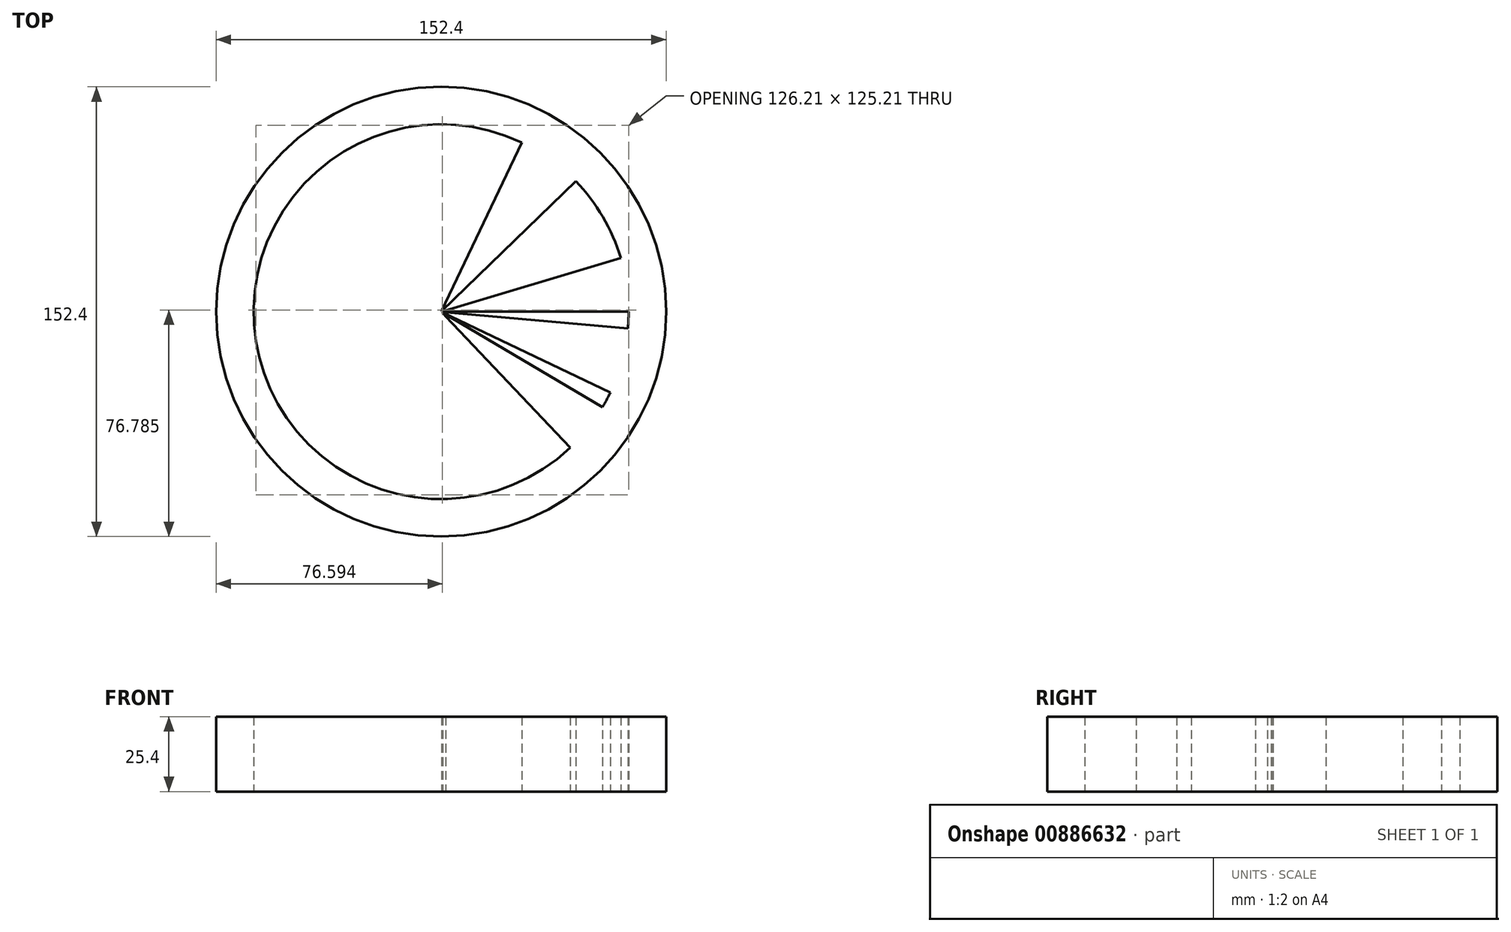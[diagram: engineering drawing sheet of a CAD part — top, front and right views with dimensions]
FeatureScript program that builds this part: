
annotation { "Feature Type Name" : "Feature", "Feature Type Description" : "" }
export const myFeature = defineFeature(function(context is Context, id is Id, definition is map)
    precondition{}
    {
        {
            var Q0;
            Q0=qCreatedBy(makeId("Top.planeOp"),FACE);
            var sketch = newSketch(context, id + "F0", { "sketchPlane" : qUnion([Q0])});
            skCircle(sketch, "E0", {"center": v(0, 0) * mm, "radius": 76.2 * mm});
            skLineSegment(sketch, "E1", {"start": v(0, 76.2) * mm, "end": v(0, -76.2) * mm});
            skLineSegment(sketch, "E2", {"start": v(-76.2, 0) * mm, "end": v(76.2, 0) * mm});
            skLineSegment(sketch, "E3", {"start": v(0, -76.2) * mm, "end": v(76.2, 0) * mm, "construction": true});
            skLineSegment(sketch, "E4", {"start": v(-76.2, 0) * mm, "end": v(0, 76.2) * mm, "construction": true});
            skLineSegment(sketch, "E5", {"start": v(-52.47, 55.26) * mm, "end": v(52.47, -55.26) * mm});
            skLineSegment(sketch, "E6", {"start": v(54.71, 53.04) * mm, "end": v(-54.71, -53.04) * mm});
            skLineSegment(sketch, "E7", {"start": v(26.69, 71.37) * mm, "end": v(-26.69, -71.37) * mm});
            skLineSegment(sketch, "E8", {"start": v(-29.5, 70.26) * mm, "end": v(29.5, -70.26) * mm});
            skLineSegment(sketch, "E9", {"start": v(71.21, 27.12) * mm, "end": v(-71.21, -27.12) * mm});
            skLineSegment(sketch, "E10", {"start": v(-68.73, 32.9) * mm, "end": v(68.73, -32.9) * mm});
            skCircle(sketch, "E11", {"center": v(0, 0) * mm, "radius": 63.5 * mm});
            skLineSegment(sketch, "E12", {"start": v(-59.38, -47.75) * mm, "end": v(59.38, 47.75) * mm});
            skLineSegment(sketch, "E13", {"start": v(-73, -21.87) * mm, "end": v(73, 21.87) * mm});
            skLineSegment(sketch, "E14", {"start": v(-75.9, 6.85) * mm, "end": v(75.9, -6.85) * mm});
            skLineSegment(sketch, "E15", {"start": v(-65.57, 38.81) * mm, "end": v(65.57, -38.81) * mm});
            skLineSegment(sketch, "E16", {"start": v(-46.6, 60.29) * mm, "end": v(46.96, -60.01) * mm});
            skLineSegment(sketch, "E17", {"start": v(-25.62, 71.76) * mm, "end": v(25.62, -71.76) * mm});
            skLineSegment(sketch, "E18", {"start": v(5.1, 76.03) * mm, "end": v(-5.1, -76.03) * mm});
            skLineSegment(sketch, "E19", {"start": v(32.75, 68.8) * mm, "end": v(-32.75, -68.8) * mm});
            skSolve(sketch);
        }
        {
            var Q0;
            {var subQ0=sQuery(id+"F0.wireOp",EDGE,"E5");var subQ1=sQuery(id+"F0.wireOp",EDGE,"E0");var subQ2=makeQuery(id+"F0.imprint","INTERSECT",VERTEX,{"disambiguationData":[OD(0.0)],"derivedFrom":[subQ1,subQ0]});Q0=makeQuery(id+"F0.imprint","IMPRINT",FACE,{"disambiguationData":[TD([[makeQuery(id+"F0.imprint","IMPRINT",EDGE,{"disambiguationData":[TD([[subQ2,-1.0]])],"derivedFrom":subQ1}),1.0]])]});}
            var Q1;
            {var subQ0=sQuery(id+"F0.wireOp",EDGE,"E5");var subQ1=sQuery(id+"F0.wireOp",EDGE,"E0");var subQ2=makeQuery(id+"F0.imprint","INTERSECT",VERTEX,{"disambiguationData":[OD(0.0)],"derivedFrom":[subQ1,subQ0]});Q1=makeQuery(id+"F0.imprint","IMPRINT",FACE,{"disambiguationData":[TD([[makeQuery(id+"F0.imprint","IMPRINT",EDGE,{"disambiguationData":[TD([[subQ2,1.0]])],"derivedFrom":subQ1}),1.0]])]});}
            var Q2;
            {var subQ0=sQuery(id+"F0.wireOp",EDGE,"E8");var subQ1=sQuery(id+"F0.wireOp",EDGE,"E0");var subQ2=makeQuery(id+"F0.imprint","INTERSECT",VERTEX,{"disambiguationData":[OD(0.0)],"derivedFrom":[subQ1,subQ0]});Q2=makeQuery(id+"F0.imprint","IMPRINT",FACE,{"disambiguationData":[TD([[makeQuery(id+"F0.imprint","IMPRINT",EDGE,{"disambiguationData":[TD([[subQ2,-1.0]])],"derivedFrom":subQ1}),1.0]])]});}
            var Q3;
            {var subQ0=sQuery(id+"F0.wireOp",EDGE,"E8");var subQ1=sQuery(id+"F0.wireOp",EDGE,"E0");var subQ2=makeQuery(id+"F0.imprint","INTERSECT",VERTEX,{"disambiguationData":[OD(0.0)],"derivedFrom":[subQ1,subQ0]});Q3=makeQuery(id+"F0.imprint","IMPRINT",FACE,{"disambiguationData":[TD([[makeQuery(id+"F0.imprint","IMPRINT",EDGE,{"disambiguationData":[TD([[subQ2,1.0]])],"derivedFrom":subQ1}),1.0]])]});}
            var Q4;
            {var subQ0=sQuery(id+"F0.wireOp",EDGE,"E1");var subQ1=sQuery(id+"F0.wireOp",EDGE,"E0");var subQ2=makeQuery(id+"F0.imprint","INTERSECT",VERTEX,{"disambiguationData":[OD(0.0)],"derivedFrom":[subQ1,subQ0]});Q4=makeQuery(id+"F0.imprint","IMPRINT",FACE,{"disambiguationData":[TD([[makeQuery(id+"F0.imprint","IMPRINT",EDGE,{"disambiguationData":[TD([[subQ2,-1.0]])],"derivedFrom":subQ1}),1.0]])]});}
            var Q5;
            {var subQ0=sQuery(id+"F0.wireOp",EDGE,"E1");var subQ1=sQuery(id+"F0.wireOp",EDGE,"E0");var subQ2=makeQuery(id+"F0.imprint","INTERSECT",VERTEX,{"disambiguationData":[OD(0.0)],"derivedFrom":[subQ1,subQ0]});Q5=makeQuery(id+"F0.imprint","IMPRINT",FACE,{"disambiguationData":[TD([[makeQuery(id+"F0.imprint","IMPRINT",EDGE,{"disambiguationData":[TD([[subQ2,1.0]])],"derivedFrom":subQ1}),1.0]])]});}
            var Q6;
            {var subQ0=sQuery(id+"F0.wireOp",EDGE,"E7");var subQ1=sQuery(id+"F0.wireOp",EDGE,"E0");var subQ2=makeQuery(id+"F0.imprint","INTERSECT",VERTEX,{"disambiguationData":[OD(0.0)],"derivedFrom":[subQ1,subQ0]});Q6=makeQuery(id+"F0.imprint","IMPRINT",FACE,{"disambiguationData":[TD([[makeQuery(id+"F0.imprint","IMPRINT",EDGE,{"disambiguationData":[TD([[subQ2,-1.0]])],"derivedFrom":subQ1}),1.0]])]});}
            var Q7;
            {var subQ0=sQuery(id+"F0.wireOp",EDGE,"E7");var subQ1=sQuery(id+"F0.wireOp",EDGE,"E0");var subQ2=makeQuery(id+"F0.imprint","INTERSECT",VERTEX,{"disambiguationData":[OD(0.0)],"derivedFrom":[subQ1,subQ0]});Q7=makeQuery(id+"F0.imprint","IMPRINT",FACE,{"disambiguationData":[TD([[makeQuery(id+"F0.imprint","IMPRINT",EDGE,{"disambiguationData":[TD([[subQ2,1.0]])],"derivedFrom":subQ1}),1.0]])]});}
            var Q8;
            {var subQ0=sQuery(id+"F0.wireOp",EDGE,"E6");var subQ1=sQuery(id+"F0.wireOp",EDGE,"E0");var subQ2=makeQuery(id+"F0.imprint","INTERSECT",VERTEX,{"disambiguationData":[OD(0.0)],"derivedFrom":[subQ1,subQ0]});Q8=makeQuery(id+"F0.imprint","IMPRINT",FACE,{"disambiguationData":[TD([[makeQuery(id+"F0.imprint","IMPRINT",EDGE,{"disambiguationData":[TD([[subQ2,-1.0]])],"derivedFrom":subQ1}),1.0]])]});}
            var Q9;
            {var subQ0=sQuery(id+"F0.wireOp",EDGE,"E6");var subQ1=sQuery(id+"F0.wireOp",EDGE,"E0");var subQ2=makeQuery(id+"F0.imprint","INTERSECT",VERTEX,{"disambiguationData":[OD(0.0)],"derivedFrom":[subQ1,subQ0]});Q9=makeQuery(id+"F0.imprint","IMPRINT",FACE,{"disambiguationData":[TD([[makeQuery(id+"F0.imprint","IMPRINT",EDGE,{"disambiguationData":[TD([[subQ2,1.0]])],"derivedFrom":subQ1}),1.0]])]});}
            var Q10;
            {var subQ0=sQuery(id+"F0.wireOp",EDGE,"E9");var subQ1=sQuery(id+"F0.wireOp",EDGE,"E0");var subQ2=makeQuery(id+"F0.imprint","INTERSECT",VERTEX,{"disambiguationData":[OD(0.0)],"derivedFrom":[subQ1,subQ0]});Q10=makeQuery(id+"F0.imprint","IMPRINT",FACE,{"disambiguationData":[TD([[makeQuery(id+"F0.imprint","IMPRINT",EDGE,{"disambiguationData":[TD([[subQ2,-1.0]])],"derivedFrom":subQ1}),1.0]])]});}
            var Q11;
            {var subQ0=sQuery(id+"F0.wireOp",EDGE,"E9");var subQ1=sQuery(id+"F0.wireOp",EDGE,"E0");var subQ2=makeQuery(id+"F0.imprint","INTERSECT",VERTEX,{"disambiguationData":[OD(0.0)],"derivedFrom":[subQ1,subQ0]});Q11=makeQuery(id+"F0.imprint","IMPRINT",FACE,{"disambiguationData":[TD([[makeQuery(id+"F0.imprint","IMPRINT",EDGE,{"disambiguationData":[TD([[subQ2,1.0]])],"derivedFrom":subQ1}),1.0]])]});}
            var Q12;
            {var subQ0=sQuery(id+"F0.wireOp",EDGE,"E2");var subQ1=sQuery(id+"F0.wireOp",EDGE,"E0");var subQ2=makeQuery(id+"F0.imprint","INTERSECT",VERTEX,{"disambiguationData":[OD(1.0)],"derivedFrom":[subQ1,subQ0]});Q12=makeQuery(id+"F0.imprint","IMPRINT",FACE,{"disambiguationData":[TD([[makeQuery(id+"F0.imprint","IMPRINT",EDGE,{"disambiguationData":[TD([[subQ2,-1.0]])],"derivedFrom":subQ1}),1.0]])]});}
            var Q13;
            {var subQ0=sQuery(id+"F0.wireOp",EDGE,"E2");var subQ1=sQuery(id+"F0.wireOp",EDGE,"E0");var subQ2=makeQuery(id+"F0.imprint","INTERSECT",VERTEX,{"disambiguationData":[OD(1.0)],"derivedFrom":[subQ1,subQ0]});Q13=makeQuery(id+"F0.imprint","IMPRINT",FACE,{"disambiguationData":[TD([[makeQuery(id+"F0.imprint","IMPRINT",EDGE,{"disambiguationData":[TD([[subQ2,1.0]])],"derivedFrom":subQ1}),1.0]])]});}
            var Q14;
            {var subQ0=sQuery(id+"F0.wireOp",EDGE,"E10");var subQ1=sQuery(id+"F0.wireOp",EDGE,"E0");var subQ2=makeQuery(id+"F0.imprint","INTERSECT",VERTEX,{"disambiguationData":[OD(1.0)],"derivedFrom":[subQ1,subQ0]});Q14=makeQuery(id+"F0.imprint","IMPRINT",FACE,{"disambiguationData":[TD([[makeQuery(id+"F0.imprint","IMPRINT",EDGE,{"disambiguationData":[TD([[subQ2,-1.0]])],"derivedFrom":subQ1}),1.0]])]});}
            var Q15;
            {var subQ0=sQuery(id+"F0.wireOp",EDGE,"E10");var subQ1=sQuery(id+"F0.wireOp",EDGE,"E0");var subQ2=makeQuery(id+"F0.imprint","INTERSECT",VERTEX,{"disambiguationData":[OD(1.0)],"derivedFrom":[subQ1,subQ0]});Q15=makeQuery(id+"F0.imprint","IMPRINT",FACE,{"disambiguationData":[TD([[makeQuery(id+"F0.imprint","IMPRINT",EDGE,{"disambiguationData":[TD([[subQ2,1.0]])],"derivedFrom":subQ1}),1.0]])]});}
            var Q16;
            {var subQ0=sQuery(id+"F0.wireOp",EDGE,"E5");var subQ1=sQuery(id+"F0.wireOp",EDGE,"E0");var subQ2=makeQuery(id+"F0.imprint","INTERSECT",VERTEX,{"disambiguationData":[OD(1.0)],"derivedFrom":[subQ1,subQ0]});Q16=makeQuery(id+"F0.imprint","IMPRINT",FACE,{"disambiguationData":[TD([[makeQuery(id+"F0.imprint","IMPRINT",EDGE,{"disambiguationData":[TD([[subQ2,-1.0]])],"derivedFrom":subQ1}),1.0]])]});}
            var Q17;
            {var subQ0=sQuery(id+"F0.wireOp",EDGE,"E5");var subQ1=sQuery(id+"F0.wireOp",EDGE,"E0");var subQ2=makeQuery(id+"F0.imprint","INTERSECT",VERTEX,{"disambiguationData":[OD(1.0)],"derivedFrom":[subQ1,subQ0]});Q17=makeQuery(id+"F0.imprint","IMPRINT",FACE,{"disambiguationData":[TD([[makeQuery(id+"F0.imprint","IMPRINT",EDGE,{"disambiguationData":[TD([[subQ2,1.0]])],"derivedFrom":subQ1}),1.0]])]});}
            var Q18;
            {var subQ0=sQuery(id+"F0.wireOp",EDGE,"E8");var subQ1=sQuery(id+"F0.wireOp",EDGE,"E0");var subQ2=makeQuery(id+"F0.imprint","INTERSECT",VERTEX,{"disambiguationData":[OD(1.0)],"derivedFrom":[subQ1,subQ0]});Q18=makeQuery(id+"F0.imprint","IMPRINT",FACE,{"disambiguationData":[TD([[makeQuery(id+"F0.imprint","IMPRINT",EDGE,{"disambiguationData":[TD([[subQ2,-1.0]])],"derivedFrom":subQ1}),1.0]])]});}
            var Q19;
            {var subQ0=sQuery(id+"F0.wireOp",EDGE,"E8");var subQ1=sQuery(id+"F0.wireOp",EDGE,"E0");var subQ2=makeQuery(id+"F0.imprint","INTERSECT",VERTEX,{"disambiguationData":[OD(1.0)],"derivedFrom":[subQ1,subQ0]});Q19=makeQuery(id+"F0.imprint","IMPRINT",FACE,{"disambiguationData":[TD([[makeQuery(id+"F0.imprint","IMPRINT",EDGE,{"disambiguationData":[TD([[subQ2,1.0]])],"derivedFrom":subQ1}),1.0]])]});}
            var Q20;
            {var subQ0=sQuery(id+"F0.wireOp",EDGE,"E1");var subQ1=sQuery(id+"F0.wireOp",EDGE,"E0");var subQ2=makeQuery(id+"F0.imprint","INTERSECT",VERTEX,{"disambiguationData":[OD(1.0)],"derivedFrom":[subQ1,subQ0]});Q20=makeQuery(id+"F0.imprint","IMPRINT",FACE,{"disambiguationData":[TD([[makeQuery(id+"F0.imprint","IMPRINT",EDGE,{"disambiguationData":[TD([[subQ2,-1.0]])],"derivedFrom":subQ1}),1.0]])]});}
            var Q21;
            {var subQ0=sQuery(id+"F0.wireOp",EDGE,"E1");var subQ1=sQuery(id+"F0.wireOp",EDGE,"E0");var subQ2=makeQuery(id+"F0.imprint","INTERSECT",VERTEX,{"disambiguationData":[OD(1.0)],"derivedFrom":[subQ1,subQ0]});Q21=makeQuery(id+"F0.imprint","IMPRINT",FACE,{"disambiguationData":[TD([[makeQuery(id+"F0.imprint","IMPRINT",EDGE,{"disambiguationData":[TD([[subQ2,1.0]])],"derivedFrom":subQ1}),1.0]])]});}
            var Q22;
            {var subQ0=sQuery(id+"F0.wireOp",EDGE,"E7");var subQ1=sQuery(id+"F0.wireOp",EDGE,"E0");var subQ2=makeQuery(id+"F0.imprint","INTERSECT",VERTEX,{"disambiguationData":[OD(1.0)],"derivedFrom":[subQ1,subQ0]});Q22=makeQuery(id+"F0.imprint","IMPRINT",FACE,{"disambiguationData":[TD([[makeQuery(id+"F0.imprint","IMPRINT",EDGE,{"disambiguationData":[TD([[subQ2,-1.0]])],"derivedFrom":subQ1}),1.0]])]});}
            var Q23;
            {var subQ0=sQuery(id+"F0.wireOp",EDGE,"E7");var subQ1=sQuery(id+"F0.wireOp",EDGE,"E0");var subQ2=makeQuery(id+"F0.imprint","INTERSECT",VERTEX,{"disambiguationData":[OD(1.0)],"derivedFrom":[subQ1,subQ0]});Q23=makeQuery(id+"F0.imprint","IMPRINT",FACE,{"disambiguationData":[TD([[makeQuery(id+"F0.imprint","IMPRINT",EDGE,{"disambiguationData":[TD([[subQ2,1.0]])],"derivedFrom":subQ1}),1.0]])]});}
            var Q24;
            {var subQ0=sQuery(id+"F0.wireOp",EDGE,"E6");var subQ1=sQuery(id+"F0.wireOp",EDGE,"E0");var subQ2=makeQuery(id+"F0.imprint","INTERSECT",VERTEX,{"disambiguationData":[OD(1.0)],"derivedFrom":[subQ1,subQ0]});Q24=makeQuery(id+"F0.imprint","IMPRINT",FACE,{"disambiguationData":[TD([[makeQuery(id+"F0.imprint","IMPRINT",EDGE,{"disambiguationData":[TD([[subQ2,-1.0]])],"derivedFrom":subQ1}),1.0]])]});}
            var Q25;
            {var subQ0=sQuery(id+"F0.wireOp",EDGE,"E9");var subQ1=sQuery(id+"F0.wireOp",EDGE,"E0");var subQ2=makeQuery(id+"F0.imprint","INTERSECT",VERTEX,{"disambiguationData":[OD(1.0)],"derivedFrom":[subQ1,subQ0]});Q25=makeQuery(id+"F0.imprint","IMPRINT",FACE,{"disambiguationData":[TD([[makeQuery(id+"F0.imprint","IMPRINT",EDGE,{"disambiguationData":[TD([[subQ2,-1.0]])],"derivedFrom":subQ1}),1.0]])]});}
            var Q26;
            {var subQ0=sQuery(id+"F0.wireOp",EDGE,"E2");var subQ1=sQuery(id+"F0.wireOp",EDGE,"E0");var subQ2=makeQuery(id+"F0.imprint","INTERSECT",VERTEX,{"disambiguationData":[OD(0.0)],"derivedFrom":[subQ1,subQ0]});Q26=makeQuery(id+"F0.imprint","IMPRINT",FACE,{"disambiguationData":[TD([[makeQuery(id+"F0.imprint","IMPRINT",EDGE,{"disambiguationData":[TD([[subQ2,-1.0]])],"derivedFrom":subQ1}),1.0]])]});}
            var Q27;
            {var subQ0=sQuery(id+"F0.wireOp",EDGE,"E10");var subQ1=sQuery(id+"F0.wireOp",EDGE,"E0");var subQ2=makeQuery(id+"F0.imprint","INTERSECT",VERTEX,{"disambiguationData":[OD(0.0)],"derivedFrom":[subQ1,subQ0]});Q27=makeQuery(id+"F0.imprint","IMPRINT",FACE,{"disambiguationData":[TD([[makeQuery(id+"F0.imprint","IMPRINT",EDGE,{"disambiguationData":[TD([[subQ2,-1.0]])],"derivedFrom":subQ1}),1.0]])]});}
            var Q28;
            {var subQ0=sQuery(id+"F0.wireOp",EDGE,"E6");var subQ1=sQuery(id+"F0.wireOp",EDGE,"E0");var subQ2=makeQuery(id+"F0.imprint","INTERSECT",VERTEX,{"disambiguationData":[OD(1.0)],"derivedFrom":[subQ1,subQ0]});Q28=makeQuery(id+"F0.imprint","IMPRINT",FACE,{"disambiguationData":[TD([[makeQuery(id+"F0.imprint","IMPRINT",EDGE,{"disambiguationData":[TD([[subQ2,1.0]])],"derivedFrom":subQ1}),1.0]])]});}
            var Q29;
            {var subQ0=sQuery(id+"F0.wireOp",EDGE,"E9");var subQ1=sQuery(id+"F0.wireOp",EDGE,"E0");var subQ2=makeQuery(id+"F0.imprint","INTERSECT",VERTEX,{"disambiguationData":[OD(1.0)],"derivedFrom":[subQ1,subQ0]});Q29=makeQuery(id+"F0.imprint","IMPRINT",FACE,{"disambiguationData":[TD([[makeQuery(id+"F0.imprint","IMPRINT",EDGE,{"disambiguationData":[TD([[subQ2,1.0]])],"derivedFrom":subQ1}),1.0]])]});}
            var Q30;
            {var subQ0=sQuery(id+"F0.wireOp",EDGE,"E2");var subQ1=sQuery(id+"F0.wireOp",EDGE,"E0");var subQ2=makeQuery(id+"F0.imprint","INTERSECT",VERTEX,{"disambiguationData":[OD(0.0)],"derivedFrom":[subQ1,subQ0]});Q30=makeQuery(id+"F0.imprint","IMPRINT",FACE,{"disambiguationData":[TD([[makeQuery(id+"F0.imprint","IMPRINT",EDGE,{"disambiguationData":[TD([[subQ2,1.0]])],"derivedFrom":subQ1}),1.0]])]});}
            var Q31;
            {var subQ0=sQuery(id+"F0.wireOp",EDGE,"E10");var subQ1=sQuery(id+"F0.wireOp",EDGE,"E0");var subQ2=makeQuery(id+"F0.imprint","INTERSECT",VERTEX,{"disambiguationData":[OD(0.0)],"derivedFrom":[subQ1,subQ0]});Q31=makeQuery(id+"F0.imprint","IMPRINT",FACE,{"disambiguationData":[TD([[makeQuery(id+"F0.imprint","IMPRINT",EDGE,{"disambiguationData":[TD([[subQ2,1.0]])],"derivedFrom":subQ1}),1.0]])]});}
            extrude(context, id + "F1", {"entities" : qUnion([Q0, Q1, Q2, Q3, Q4, Q5, Q6, Q7, Q8, Q9, Q10, Q11, Q12, Q13, Q14, Q15, Q16, Q17, Q18, Q19, Q20, Q21, Q22, Q23, Q24, Q25, Q26, Q27, Q28, Q29, Q30, Q31]), "depth" : 25.4 * mm, "offsetDistance" : 25.4 * mm});
        }
        {
            var Q0;
            {var subQ0=sQuery(id+"F0.wireOp",EDGE,"E11");var subQ1=sQuery(id+"F0.wireOp",EDGE,"E8");var subQ2=makeQuery(id+"F0.imprint","INTERSECT",VERTEX,{"disambiguationData":[OD(0.0)],"derivedFrom":[subQ1,subQ0]});Q0=makeQuery(id+"F0.imprint","IMPRINT",FACE,{"disambiguationData":[TD([[makeQuery(id+"F0.imprint","IMPRINT",EDGE,{"disambiguationData":[TD([[subQ2,-1.0]])],"derivedFrom":subQ1}),-1.0]])]});}
            var Q1;
            {var subQ0=sQuery(id+"F0.wireOp",EDGE,"E11");var subQ1=sQuery(id+"F0.wireOp",EDGE,"E1");var subQ2=makeQuery(id+"F0.imprint","INTERSECT",VERTEX,{"disambiguationData":[OD(0.0)],"derivedFrom":[subQ1,subQ0]});Q1=makeQuery(id+"F0.imprint","IMPRINT",FACE,{"disambiguationData":[TD([[makeQuery(id+"F0.imprint","IMPRINT",EDGE,{"disambiguationData":[TD([[subQ2,-1.0]])],"derivedFrom":subQ1}),-1.0]])]});}
            var Q2;
            {var subQ0=sQuery(id+"F0.wireOp",EDGE,"E11");var subQ1=sQuery(id+"F0.wireOp",EDGE,"E7");var subQ2=makeQuery(id+"F0.imprint","INTERSECT",VERTEX,{"disambiguationData":[OD(0.0)],"derivedFrom":[subQ1,subQ0]});Q2=makeQuery(id+"F0.imprint","IMPRINT",FACE,{"disambiguationData":[TD([[makeQuery(id+"F0.imprint","IMPRINT",EDGE,{"disambiguationData":[TD([[subQ2,-1.0]])],"derivedFrom":subQ1}),-1.0]])]});}
            var Q3;
            {var subQ0=sQuery(id+"F0.wireOp",EDGE,"E11");var subQ1=sQuery(id+"F0.wireOp",EDGE,"E6");var subQ2=makeQuery(id+"F0.imprint","INTERSECT",VERTEX,{"disambiguationData":[OD(0.0)],"derivedFrom":[subQ1,subQ0]});Q3=makeQuery(id+"F0.imprint","IMPRINT",FACE,{"disambiguationData":[TD([[makeQuery(id+"F0.imprint","IMPRINT",EDGE,{"disambiguationData":[TD([[subQ2,-1.0]])],"derivedFrom":subQ1}),-1.0]])]});}
            var Q4;
            {var subQ0=sQuery(id+"F0.wireOp",EDGE,"E11");var subQ1=sQuery(id+"F0.wireOp",EDGE,"E9");var subQ2=makeQuery(id+"F0.imprint","INTERSECT",VERTEX,{"disambiguationData":[OD(0.0)],"derivedFrom":[subQ1,subQ0]});Q4=makeQuery(id+"F0.imprint","IMPRINT",FACE,{"disambiguationData":[TD([[makeQuery(id+"F0.imprint","IMPRINT",EDGE,{"disambiguationData":[TD([[subQ2,-1.0]])],"derivedFrom":subQ1}),-1.0]])]});}
            var Q5;
            {var subQ0=sQuery(id+"F0.wireOp",EDGE,"E16");var subQ1=sQuery(id+"F0.wireOp",EDGE,"E2");var subQ2=makeQuery(id+"F0.imprint","INTERSECT",VERTEX,{"derivedFrom":[subQ1,subQ0]});Q5=makeQuery(id+"F0.imprint","IMPRINT",FACE,{"disambiguationData":[TD([[makeQuery(id+"F0.imprint","IMPRINT",EDGE,{"disambiguationData":[TD([[subQ2,-1.0]])],"derivedFrom":subQ1}),1.0]])]});}
            var Q6;
            {var subQ0=sQuery(id+"F0.wireOp",EDGE,"E16");var subQ1=sQuery(id+"F0.wireOp",EDGE,"E10");var subQ2=makeQuery(id+"F0.imprint","INTERSECT",VERTEX,{"derivedFrom":[subQ1,subQ0]});Q6=makeQuery(id+"F0.imprint","IMPRINT",FACE,{"disambiguationData":[TD([[makeQuery(id+"F0.imprint","IMPRINT",EDGE,{"disambiguationData":[TD([[subQ2,-1.0]])],"derivedFrom":subQ1}),1.0]])]});}
            var Q7;
            {var subQ0=sQuery(id+"F0.wireOp",EDGE,"E16");var subQ1=sQuery(id+"F0.wireOp",EDGE,"E5");var subQ2=makeQuery(id+"F0.imprint","INTERSECT",VERTEX,{"derivedFrom":[subQ1,subQ0]});Q7=makeQuery(id+"F0.imprint","IMPRINT",FACE,{"disambiguationData":[TD([[makeQuery(id+"F0.imprint","IMPRINT",EDGE,{"disambiguationData":[TD([[subQ2,-1.0]])],"derivedFrom":subQ1}),1.0]])]});}
            extrude(context, id + "F2", {"entities" : qUnion([Q0, Q1, Q2, Q3, Q4, Q5, Q6, Q7]), "operationType" : NewBodyOperationType.ADD, "depth" : 25.4 * mm, "offsetDistance" : 25.4 * mm});
        }
        {
            var Q0;
            {var subQ0=sQuery(id+"F0.wireOp",EDGE,"E11");var subQ1=sQuery(id+"F0.wireOp",EDGE,"E6");var subQ2=makeQuery(id+"F0.imprint","INTERSECT",VERTEX,{"disambiguationData":[OD(1.0)],"derivedFrom":[subQ1,subQ0]});Q0=makeQuery(id+"F0.imprint","IMPRINT",FACE,{"disambiguationData":[TD([[makeQuery(id+"F0.imprint","IMPRINT",EDGE,{"disambiguationData":[TD([[subQ2,-1.0]])],"derivedFrom":subQ0}),1.0]])]});}
            extrude(context, id + "F3", {"entities" : qUnion([Q0]), "operationType" : NewBodyOperationType.ADD, "depth" : 25.4 * mm, "offsetDistance" : 25.4 * mm});
        }
    });
